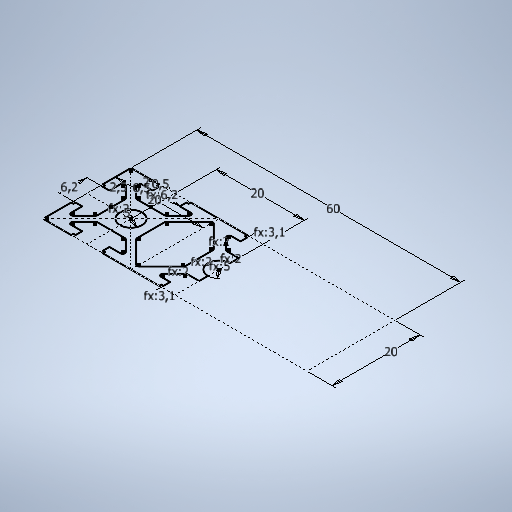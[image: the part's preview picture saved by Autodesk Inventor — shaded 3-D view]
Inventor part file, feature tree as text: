
AUTODESK INVENTOR PART (.ipt)
format: ipt  version: 2025.2 (Build 292293000, 293)  size: 322,560 bytes
history: native  units: mm
features: sketch x1
ambient origin geometry x8: Origin, YZ Plane, XZ Plane, XY Plane, X Axis, Y Axis, Z Axis, Center Point
feature tree (1):
  sketch  "Esboço1"  dims[d0=20.0mm d2=5.0mm d4=2.0mm d7=0.5mm d8=2.0mm d17=5.0mm d18=6.2mm d23=2.0mm d25=0.5mm d26=2.5mm d27=6.2mm d29=20.0mm d30=5.0mm d31=60.0mm d32=20.0mm d33=2.0mm d34=3.1mm d35=2.0mm d36=2.0mm d37=3.1mm d38=2.0mm d19=0.5mm d20=0.872665mm d39=0.5mm d40=0.872665mm d41=0.5mm d42=0.872665mm]
